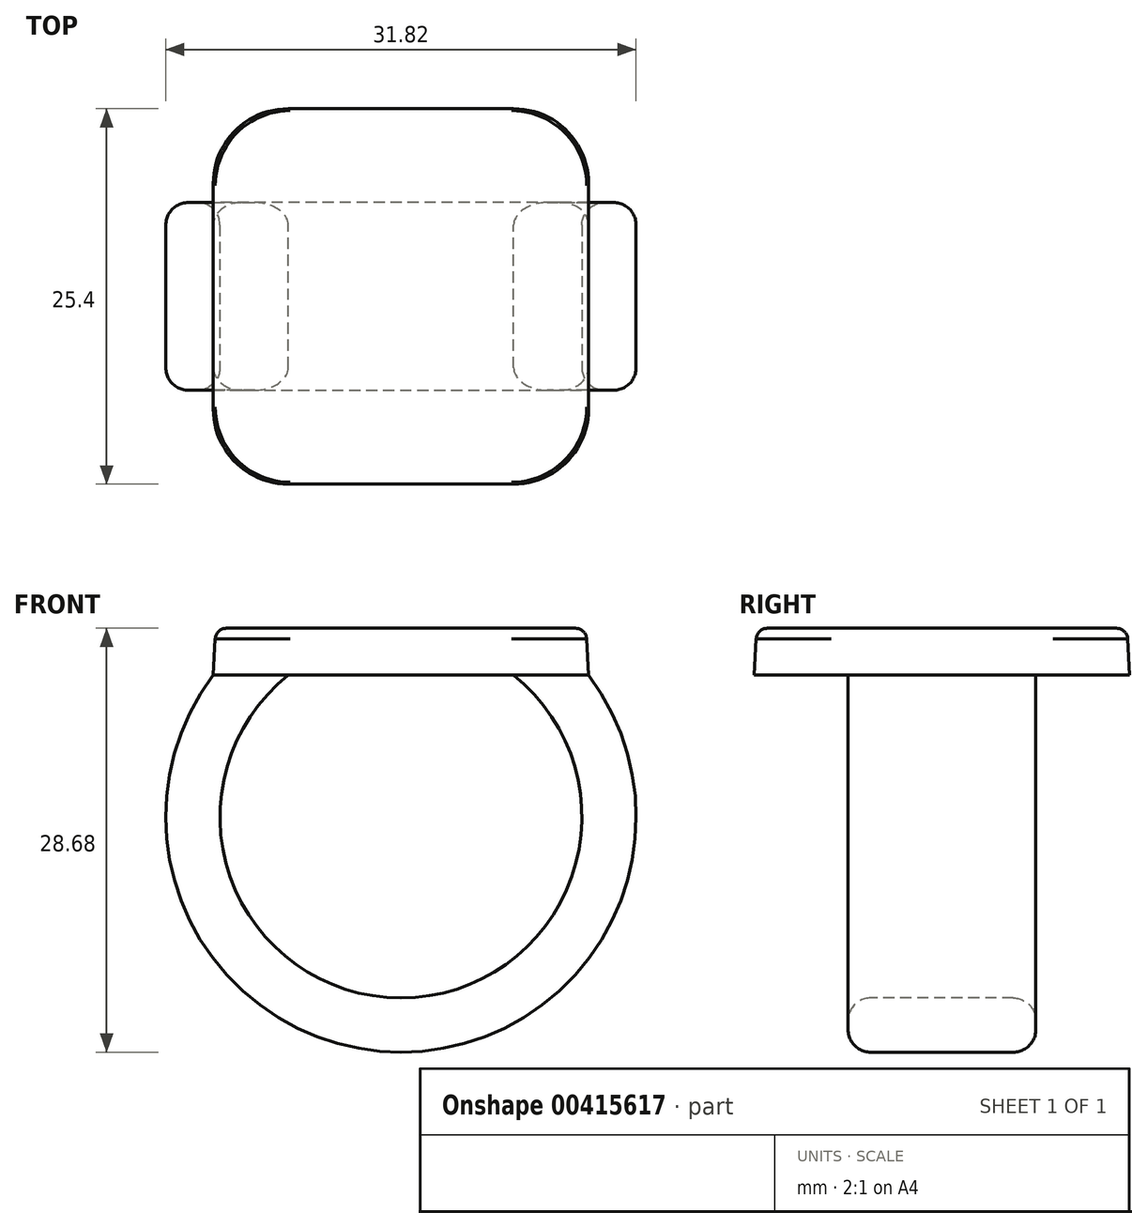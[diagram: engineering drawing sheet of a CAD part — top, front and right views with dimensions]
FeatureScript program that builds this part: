
annotation { "Feature Type Name" : "Feature", "Feature Type Description" : "" }
export const myFeature = defineFeature(function(context is Context, id is Id, definition is map)
    precondition{}
    {
        {
            var Q0;
            Q0=qCreatedBy(makeId("Top.planeOp"),FACE);
            var sketch = newSketch(context, id + "F0", { "sketchPlane" : qUnion([Q0])});
            skLineSegment(sketch, "E0.bottom", {"start": v(12.7, 12.7) * mm, "end": v(-12.7, 12.7) * mm});
            skLineSegment(sketch, "E0.top", {"start": v(12.7, -12.7) * mm, "end": v(-12.7, -12.7) * mm});
            skLineSegment(sketch, "E0.left", {"start": v(12.7, 12.7) * mm, "end": v(12.7, -12.7) * mm});
            skLineSegment(sketch, "E0.right", {"start": v(-12.7, 12.7) * mm, "end": v(-12.7, -12.7) * mm});
            skPoint(sketch, "E0.middle", {"position": v(0, 0) * mm});
            skSolve(sketch);
        }
        {
            var Q0;
            Q0 = qSketchRegion(id + "F0", true);
            extrude(context, id + "F1", {"entities" : qUnion([Q0]), "depth" : 3.17 * mm, "hasDraft" : true, "draftAngle" : 3 * degree, "draftPullDirection" : true});
        }
        {
            var Q0;
            Q0=qCreatedBy(makeId("Front.planeOp"),FACE);
            var sketch = newSketch(context, id + "F2", { "sketchPlane" : qUnion([Q0])});
            skArc(sketch, "E1", {"start": v(-10.16, 0) * mm, "mid": v(0, -23.56) * mm, "end": v(10.16, 0) * mm});
            skSolve(sketch);
        }
        {
            var Q0;
            Q0=makeQuery(id+"F1.opExtrude","CAP_FACE",FACE,{"disambiguationData":[OSD([sQuery(id+"F0.wireOp",EDGE,"E0.bottom"),sQuery(id+"F0.wireOp",EDGE,"E0.top"),sQuery(id+"F0.wireOp",EDGE,"E0.left"),sQuery(id+"F0.wireOp",EDGE,"E0.right")])],"isStart":true});
            var sketch = newSketch(context, id + "F3", { "sketchPlane" : qUnion([Q0])});
            skLineSegment(sketch, "E2.bottom", {"start": v(-12.7, 6.35) * mm, "end": v(-7.62, 6.35) * mm});
            skLineSegment(sketch, "E2.top", {"start": v(-12.7, -6.35) * mm, "end": v(-7.62, -6.35) * mm});
            skLineSegment(sketch, "E2.left", {"start": v(-12.7, 6.35) * mm, "end": v(-12.7, -6.35) * mm});
            skLineSegment(sketch, "E2.right", {"start": v(-7.62, 6.35) * mm, "end": v(-7.62, -6.35) * mm});
            skPoint(sketch, "E2.middle", {"position": v(-10.16, 0) * mm});
            skSolve(sketch);
        }
        {
            var Q0;
            Q0 = qSketchRegion(id + "F3", true);
            var Q1;
            Q1 = qConstructionFilter(qBodyType(qCreatedBy(id + "F2" ,EDGE), BodyType.WIRE), ConstructionObject.NO);
            sweep(context, id + "F4", {"operationType" : NewBodyOperationType.ADD, "profiles" : qUnion([Q0]), "path" : qUnion([Q1])});
        }
        {
            var Q0;
            Q0=qCreatedBy(makeId("Front.planeOp"),FACE);
            var sketch = newSketch(context, id + "F5", { "sketchPlane" : qUnion([Q0])});
            skLineSegment(sketch, "E3.1", {"start": v(10.01, -2.54) * mm, "end": v(10.16, 0) * mm});
            skArc(sketch, "E3.2", {"start": v(10.01, -2.54) * mm, "mid": v(8.9, -1.18) * mm, "end": v(7.62, 0) * mm});
            skPoint(sketch, "E3.0.1.end.orphan", {"position": v(12.53, 3.18) * mm});
            skPoint(sketch, "E4.orphan", {"position": v(12.7, 0) * mm});
            skLineSegment(sketch, "E5.trimOffspring", {"start": v(7.62, 0) * mm, "end": v(10.16, 0) * mm});
            skPoint(sketch, "E3.0.3.start.orphan", {"position": v(-12.53, 3.18) * mm});
            skPoint(sketch, "E3.0.0.start.orphan", {"position": v(-12.7, 0) * mm});
            skPoint(sketch, "E6.orphan", {"position": v(-7.62, 0) * mm});
            skSolve(sketch);
        }
        {
            var Q0;
            Q0 = qSketchRegion(id + "F5", true);
            var Q1;
            Q1=makeQuery(id+"F4.opSweep","SWEPT_FACE",FACE,{"disambiguationData":[OSD([sQuery(id+"F2.wireOp",EDGE,"E1"),sQuery(id+"F3.wireOp",EDGE,"E2.bottom")])]});
            var Q2;
            Q2=makeQuery(id+"F4.opSweep","SWEPT_FACE",FACE,{"disambiguationData":[OSD([sQuery(id+"F2.wireOp",EDGE,"E1"),sQuery(id+"F3.wireOp",EDGE,"E2.top")])]});
            extrude(context, id + "F6", {"entities" : qUnion([Q0]), "operationType" : NewBodyOperationType.ADD, "endBound" : BoundingType.UP_TO_SURFACE, "endBoundEntityFace" : qUnion([Q1]), "depth" : 25.4 * mm, "hasSecondDirection" : true, "secondDirectionBound" : SecondDirectionBoundingType.UP_TO_SURFACE, "secondDirectionOppositeDirection" : true, "secondDirectionBoundEntityFace" : qUnion([Q2]), "secondDirectionDepth" : 25.4 * mm});
        }
        {
            var Q0;
            Q0=makeQuery(id+"F1.opExtrude","SWEPT_EDGE",EDGE,{"disambiguationData":[OSD([sQuery(id+"F0.wireOp",EDGE,"E0.bottom"),sQuery(id+"F0.wireOp",EDGE,"E0.right")])]});
            var Q1;
            Q1=makeQuery(id+"F1.opExtrude","SWEPT_EDGE",EDGE,{"disambiguationData":[OSD([sQuery(id+"F0.wireOp",EDGE,"E0.top"),sQuery(id+"F0.wireOp",EDGE,"E0.right")])]});
            var Q2;
            Q2=makeQuery(id+"F1.opExtrude","SWEPT_EDGE",EDGE,{"disambiguationData":[OSD([sQuery(id+"F0.wireOp",EDGE,"E0.top"),sQuery(id+"F0.wireOp",EDGE,"E0.left")])]});
            var Q3;
            Q3=makeQuery(id+"F1.opExtrude","SWEPT_EDGE",EDGE,{"disambiguationData":[OSD([sQuery(id+"F0.wireOp",EDGE,"E0.bottom"),sQuery(id+"F0.wireOp",EDGE,"E0.left")])]});
            fillet(context, id + "F7", {"entities" : qUnion([Q0, Q1, Q2, Q3]), "radius" : 5.08 * mm, "tangentPropagation" : true, "allowEdgeOverflow" : false});
        }
        {
            var Q0;
            {var subQ0=sQuery(id+"F3.wireOp",EDGE,"E2.bottom");var subQ1=sQuery(id+"F2.wireOp",EDGE,"E1");Q0=makeQuery(id+"F6.boolean.opBoolean","MERGE",EDGE,{"derivedFrom":[makeQuery(id+"F4.opSweep","SWEPT_EDGE",EDGE,{"disambiguationData":[OSD([subQ1,subQ0,sQuery(id+"F3.wireOp",EDGE,"E2.right")])]}),makeQuery(id+"F6.opExtrude","TWEAK_EDGE",EDGE,{"derivedFrom":[makeQuery(id+"F4.opSweep","SWEPT_FACE",FACE,{"disambiguationData":[OSD([subQ1,subQ0])]}),makeQuery(id+"F5.imprint","IMPRINT",EDGE,{"derivedFrom":sQuery(id+"F5.wireOp",EDGE,"E3.2")})]})]});}
            var Q1;
            {var subQ0=sQuery(id+"F3.wireOp",EDGE,"E2.top");var subQ1=sQuery(id+"F2.wireOp",EDGE,"E1");Q1=makeQuery(id+"F6.boolean.opBoolean","MERGE",EDGE,{"derivedFrom":[makeQuery(id+"F4.opSweep","SWEPT_EDGE",EDGE,{"disambiguationData":[OSD([subQ1,subQ0,sQuery(id+"F3.wireOp",EDGE,"E2.right")])]}),makeQuery(id+"F6.opExtrude","TWEAK_EDGE",EDGE,{"derivedFrom":[makeQuery(id+"F4.opSweep","SWEPT_FACE",FACE,{"disambiguationData":[OSD([subQ1,subQ0])]}),makeQuery(id+"F5.imprint","IMPRINT",EDGE,{"derivedFrom":sQuery(id+"F5.wireOp",EDGE,"E3.2")})]})]});}
            var Q2;
            Q2=makeQuery(id+"F4.opSweep","SWEPT_EDGE",EDGE,{"disambiguationData":[OSD([sQuery(id+"F0.wireOp",EDGE,"E0.right"),sQuery(id+"F2.wireOp",EDGE,"E1"),sQuery(id+"F3.wireOp",EDGE,"E2.bottom"),sQuery(id+"F3.wireOp",EDGE,"E2.left")])]});
            var Q3;
            Q3=makeQuery(id+"F4.opSweep","SWEPT_EDGE",EDGE,{"disambiguationData":[OSD([sQuery(id+"F0.wireOp",EDGE,"E0.right"),sQuery(id+"F2.wireOp",EDGE,"E1"),sQuery(id+"F3.wireOp",EDGE,"E2.top"),sQuery(id+"F3.wireOp",EDGE,"E2.left")])]});
            fillet(context, id + "F8", {"entities" : qUnion([Q0, Q1, Q2, Q3]), "radius" : 1.52 * mm, "tangentPropagation" : true, "allowEdgeOverflow" : false});
        }
        {
            var Q0;
            Q0=makeQuery(id+"F1.opExtrude","CAP_FACE",FACE,{"disambiguationData":[OSD([sQuery(id+"F0.wireOp",EDGE,"E0.bottom"),sQuery(id+"F0.wireOp",EDGE,"E0.top"),sQuery(id+"F0.wireOp",EDGE,"E0.left"),sQuery(id+"F0.wireOp",EDGE,"E0.right")])],"isStart":false});
            fillet(context, id + "F9", {"entities" : qUnion([Q0]), "radius" : 0.76 * mm, "tangentPropagation" : true, "allowEdgeOverflow" : false});
        }
    });
